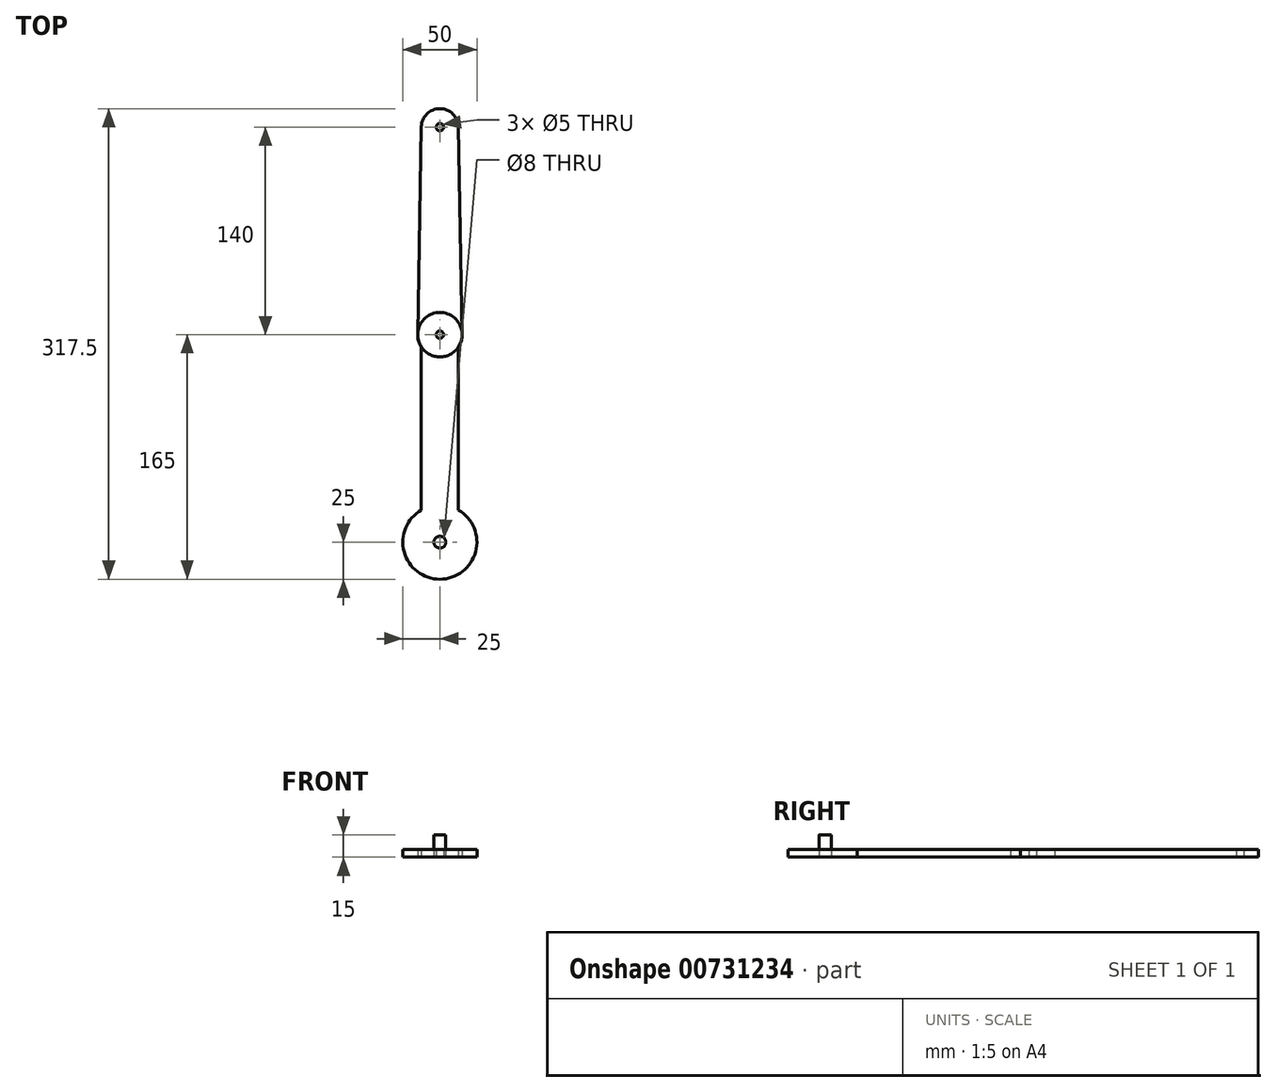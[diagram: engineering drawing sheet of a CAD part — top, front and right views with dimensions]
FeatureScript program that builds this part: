
annotation { "Feature Type Name" : "Feature", "Feature Type Description" : "" }
export const myFeature = defineFeature(function(context is Context, id is Id, definition is map)
    precondition{}
    {
        {
            var Q0;
            Q0=qCreatedBy(makeId("Top.planeOp"),FACE);
            var sketch = newSketch(context, id + "F0", { "sketchPlane" : qUnion([Q0])});
            skArc(sketch, "E0", {"start": v(-12.5, 21.65) * mm, "mid": v(0, -25) * mm, "end": v(12.5, 21.65) * mm});
            skLineSegment(sketch, "E1", {"start": v(-12.5, 21.65) * mm, "end": v(-12.5, 131.7) * mm});
            skLineSegment(sketch, "E2", {"start": v(12.5, 131.7) * mm, "end": v(12.5, 21.65) * mm});
            skLineSegment(sketch, "E3", {"start": v(0, 140) * mm, "end": v(0, 0) * mm, "construction": true});
            skArc(sketch, "E4", {"start": v(12.5, 131.7) * mm, "mid": v(0, 155) * mm, "end": v(-12.5, 131.7) * mm});
            skLineSegment(sketch, "E5", {"start": v(-12.5, 131.7) * mm, "end": v(12.5, 131.7) * mm, "construction": true});
            skPoint(sketch, "E6", {"position": v(0, 131.7) * mm});
            skCircle(sketch, "E7", {"center": v(0, 140) * mm, "radius": 2.5 * mm});
            skCircle(sketch, "E8", {"center": v(0, 0) * mm, "radius": 4 * mm});
            skSolve(sketch);
        }
        {
            var Q0;
            Q0=makeQuery(id+"F0.imprint","IMPRINT",FACE,{"disambiguationData":[TD([[makeQuery(id+"F0.imprint","IMPRINT",EDGE,{"derivedFrom":sQuery(id+"F0.wireOp",EDGE,"E0")}),1.0]])]});
            extrude(context, id + "F1", {"entities" : qUnion([Q0]), "depth" : 5 * mm, "offsetDistance" : 25 * mm});
        }
        {
            var Q0;
            Q0=qCreatedBy(makeId("Top.planeOp"),FACE);
            var sketch = newSketch(context, id + "F2", { "sketchPlane" : qUnion([Q0])});
            skCircle(sketch, "E9.0", {"center": v(0, 140) * mm, "radius": 2.5 * mm});
            skArc(sketch, "E10", {"start": v(-15, 140.27) * mm, "mid": v(0, 125) * mm, "end": v(15, 140.27) * mm});
            skLineSegment(sketch, "E11", {"start": v(0, 140) * mm, "end": v(0, 280) * mm, "construction": true});
            skCircle(sketch, "E12", {"center": v(0, 280) * mm, "radius": 2.5 * mm});
            skArc(sketch, "E13", {"start": v(12.5, 280.22) * mm, "mid": v(0, 292.5) * mm, "end": v(-12.5, 280.22) * mm});
            skLineSegment(sketch, "E14", {"start": v(-12.5, 280.22) * mm, "end": v(-15, 140.27) * mm});
            skLineSegment(sketch, "E15", {"start": v(12.5, 280.22) * mm, "end": v(15, 140.27) * mm});
            skSolve(sketch);
        }
        {
            var Q0;
            Q0=makeQuery(id+"F2.imprint","IMPRINT",FACE,{"disambiguationData":[TD([[makeQuery(id+"F2.imprint","IMPRINT",EDGE,{"derivedFrom":sQuery(id+"F2.wireOp",EDGE,"E9.0")}),-1.0]])]});
            extrude(context, id + "F3", {"entities" : qUnion([Q0]), "depth" : 5 * mm, "offsetDistance" : 25 * mm});
        }
        {
            var Q0;
            Q0=qCreatedBy(makeId("Top.planeOp"),FACE);
            var sketch = newSketch(context, id + "F4", { "sketchPlane" : qUnion([Q0])});
            skCircle(sketch, "E16.0", {"center": v(0, 0) * mm, "radius": 4 * mm});
            skSolve(sketch);
        }
        {
            var Q0;
            Q0=makeQuery(id+"F4.imprint","IMPRINT",FACE,{"disambiguationData":[TD([[makeQuery(id+"F4.imprint","IMPRINT",EDGE,{"derivedFrom":sQuery(id+"F4.wireOp",EDGE,"E16.0")}),1.0]])]});
            var Q1;
            Q1=sQuery(id+"F4.wireOp",EDGE,"E16.0");
            extrude(context, id + "F5", {"entities" : qUnion([Q0]), "surfaceEntities" : qUnion([Q1]), "depth" : 15 * mm, "offsetDistance" : 25 * mm});
        }
    });
